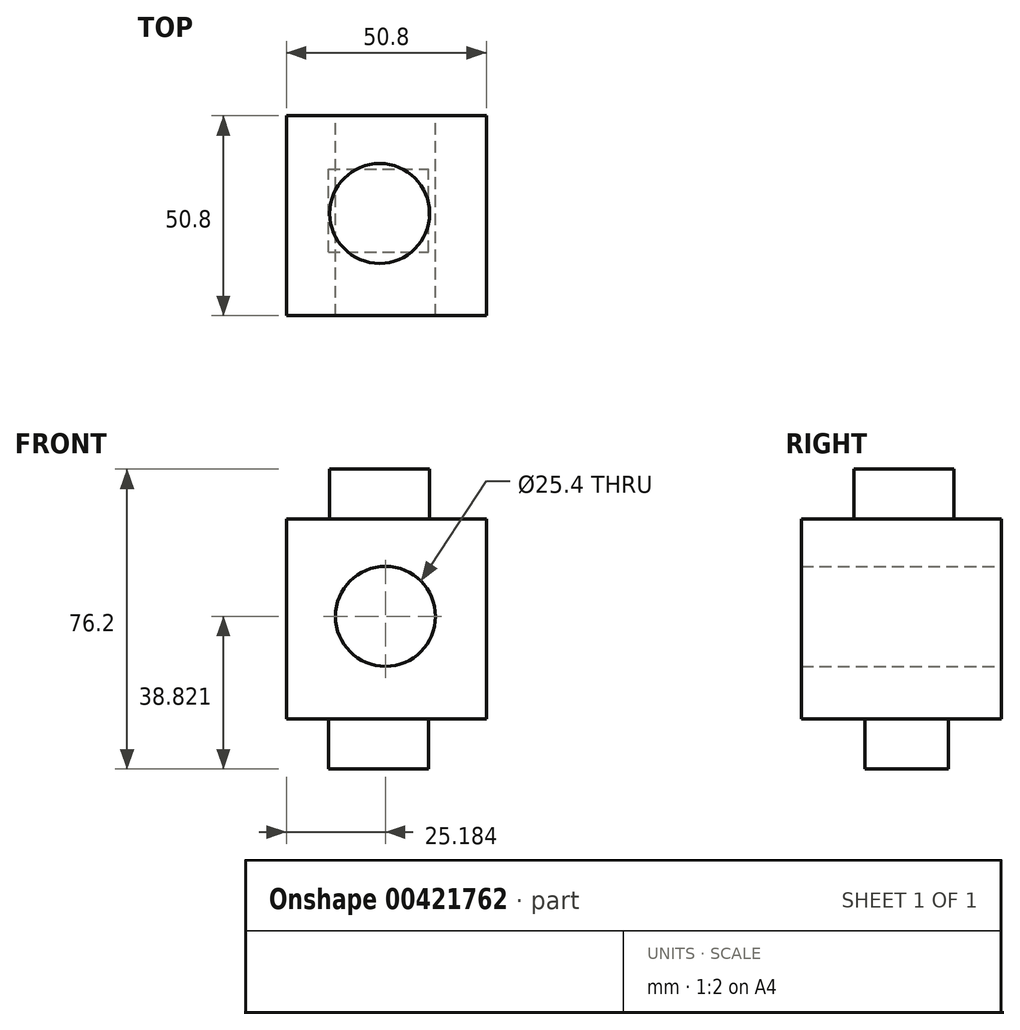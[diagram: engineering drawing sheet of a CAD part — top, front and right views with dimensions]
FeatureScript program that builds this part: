
annotation { "Feature Type Name" : "Feature", "Feature Type Description" : "" }
export const myFeature = defineFeature(function(context is Context, id is Id, definition is map)
    precondition{}
    {
        {
            var Q0;
            Q0=qCreatedBy(makeId("Front.planeOp"),FACE);
            var sketch = newSketch(context, id + "F0", { "sketchPlane" : qUnion([Q0])});
            skLineSegment(sketch, "E0", {"start": v(-36.06, 50.8) * mm, "end": v(14.74, 50.8) * mm});
            skLineSegment(sketch, "E1", {"start": v(14.74, 0) * mm, "end": v(14.74, 50.8) * mm});
            skLineSegment(sketch, "E2", {"start": v(-36.06, 50.8) * mm, "end": v(-36.06, 0) * mm});
            skLineSegment(sketch, "E3", {"start": v(-36.06, 0) * mm, "end": v(14.74, 0) * mm});
            skCircle(sketch, "E4", {"center": v(-10.88, 26.12) * mm, "radius": 12.7 * mm});
            skSolve(sketch);
        }
        {
            var Q0;
            Q0=makeQuery(id+"F0.imprint","IMPRINT",FACE,{"disambiguationData":[TD([[makeQuery(id+"F0.imprint","IMPRINT",EDGE,{"derivedFrom":sQuery(id+"F0.wireOp",EDGE,"E0")}),-1.0]])]});
            extrude(context, id + "F1", {"entities" : qUnion([Q0]), "depth" : 50.8 * mm});
        }
        {
            var Q0;
            Q0=makeQuery(id+"F1.opExtrude","SWEPT_FACE",FACE,{"disambiguationData":[OSD([sQuery(id+"F0.wireOp",EDGE,"E0")])]});
            var sketch = newSketch(context, id + "F2", { "sketchPlane" : qUnion([Q0])});
            skCircle(sketch, "E5", {"center": v(-12.35, -24.82) * mm, "radius": 12.7 * mm});
            skSolve(sketch);
        }
        {
            var Q0;
            Q0=makeQuery(id+"F2.imprint","IMPRINT",FACE,{"disambiguationData":[TD([[makeQuery(id+"F2.imprint","IMPRINT",EDGE,{"derivedFrom":sQuery(id+"F2.wireOp",EDGE,"E5")}),1.0]])]});
            extrude(context, id + "F3", {"entities" : qUnion([Q0]), "operationType" : NewBodyOperationType.ADD, "depth" : 12.7 * mm});
        }
        {
            var Q0;
            Q0=makeQuery(id+"F1.opExtrude","SWEPT_FACE",FACE,{"disambiguationData":[OSD([sQuery(id+"F0.wireOp",EDGE,"E3")])]});
            var sketch = newSketch(context, id + "F4", { "sketchPlane" : qUnion([Q0])});
            skLineSegment(sketch, "E6.bottom", {"start": v(-25.4, 34.66) * mm, "end": v(0, 34.66) * mm});
            skLineSegment(sketch, "E6.top", {"start": v(-25.4, 13.51) * mm, "end": v(0, 13.51) * mm});
            skLineSegment(sketch, "E6.left", {"start": v(-25.4, 34.66) * mm, "end": v(-25.4, 13.51) * mm});
            skLineSegment(sketch, "E6.right", {"start": v(0, 34.66) * mm, "end": v(0, 13.51) * mm});
            skSolve(sketch);
        }
        {
            var Q0;
            Q0 = qSketchRegion(id + "F4", true);
            extrude(context, id + "F5", {"entities" : qUnion([Q0]), "operationType" : NewBodyOperationType.ADD, "depth" : 12.7 * mm});
        }
    });
